# Revit family: 50-151-609_graa_simplified_rameseter
name_source: partatom
category: Generic Models
units: mm (PartAtom-declared; Revit-internal decimal feet)

## family parameters
Always vertical = Yes
Can host rebar = No
Cut with Voids When Loaded = No
Part Type = Normal
Room Calculation Point = No
Round Connector Dimension = Use Diameter
Shared = No
Work Plane-Based = No

## types (1)
- Type 1
    Artnr_graa_simplified_rameseter = 50-151-609
    CheckedDate = -
    CheckedDate_graa_simplified_rameseter = -
    Default Elevation = 0 mm  [stored 0 ft]
    Description_graa_simplified_rameseter = Huskestativ 1-seter
    Number = 14750
    Number_graa_simplified_rameseter = 14750
    PartName_graa_simplified_rameseter = Huskestativ 1-seter
    Revision = 0
    Revision_graa_simplified_rameseter = 0

note: [stored X ft] marks values corroborated as IEEE doubles in the binary element streams (Revit-internal decimal feet)

## geometry (parser evidence)
native form markers: Sweep x16
no freeform markers — native parametric forms only
